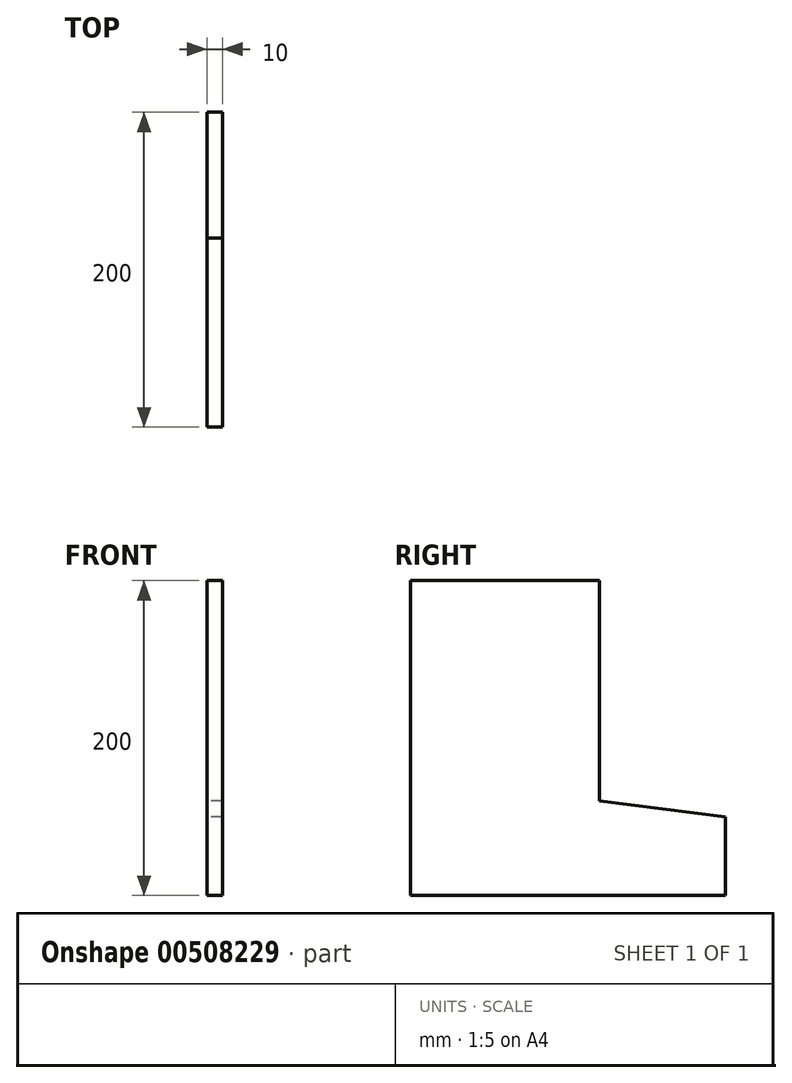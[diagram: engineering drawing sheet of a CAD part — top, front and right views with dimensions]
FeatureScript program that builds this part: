
annotation { "Feature Type Name" : "Feature", "Feature Type Description" : "" }
export const myFeature = defineFeature(function(context is Context, id is Id, definition is map)
    precondition{}
    {
        {
            var Q0;
            Q0=qCreatedBy(makeId("Right.planeOp"),FACE);
            var sketch = newSketch(context, id + "F0", { "sketchPlane" : qUnion([Q0])});
            skLineSegment(sketch, "E0", {"start": v(0, 0) * mm, "end": v(0, 200) * mm});
            skLineSegment(sketch, "E1", {"start": v(0, 0) * mm, "end": v(200, 0) * mm});
            skLineSegment(sketch, "E2", {"start": v(200, 0) * mm, "end": v(200, 50) * mm});
            skLineSegment(sketch, "E3", {"start": v(0, 200) * mm, "end": v(120, 200) * mm});
            skLineSegment(sketch, "E4", {"start": v(120, 200) * mm, "end": v(120, 60) * mm});
            skLineSegment(sketch, "E5", {"start": v(120, 60) * mm, "end": v(200, 50) * mm});
            skSolve(sketch);
        }
        {
            var Q0;
            Q0 = qSketchRegion(id + "F0", true);
            extrude(context, id + "F1", {"entities" : qUnion([Q0]), "endBound" : BoundingType.SYMMETRIC, "depth" : 10 * mm});
        }
    });
